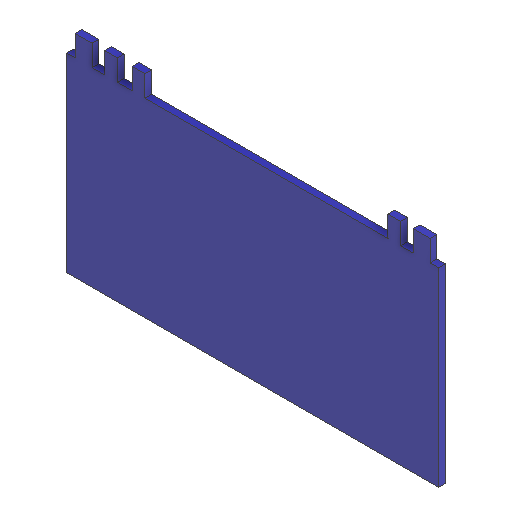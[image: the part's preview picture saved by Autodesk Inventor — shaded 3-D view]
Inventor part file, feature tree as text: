
AUTODESK INVENTOR PART (.ipt)
format: ipt  version: 2025.2 (Build 292293000, 293)  size: 123,392 bytes
history: native  units: mm
features: extrude x1, sketch x1
ambient origin geometry x8: Origin, YZ Plane, XZ Plane, XY Plane, X Axis, Y Axis, Z Axis, Center Point
bodies: Solid1 (feature_tree)
feature tree (2):
  extrude  "Extrusion1"  Depth=88.0mm
  sketch  "Sketch1"  dims[d0=45.0mm d1=88.0mm d2=4.0mm d3=3.0mm d4=3.0mm d5=3.0mm d6=4.0mm d7=2.0mm d8=3.0mm d9=3.5mm d10=2.0mm d11=3.0mm d12=5.0mm d13=1.6mm d14=0.0mm]
